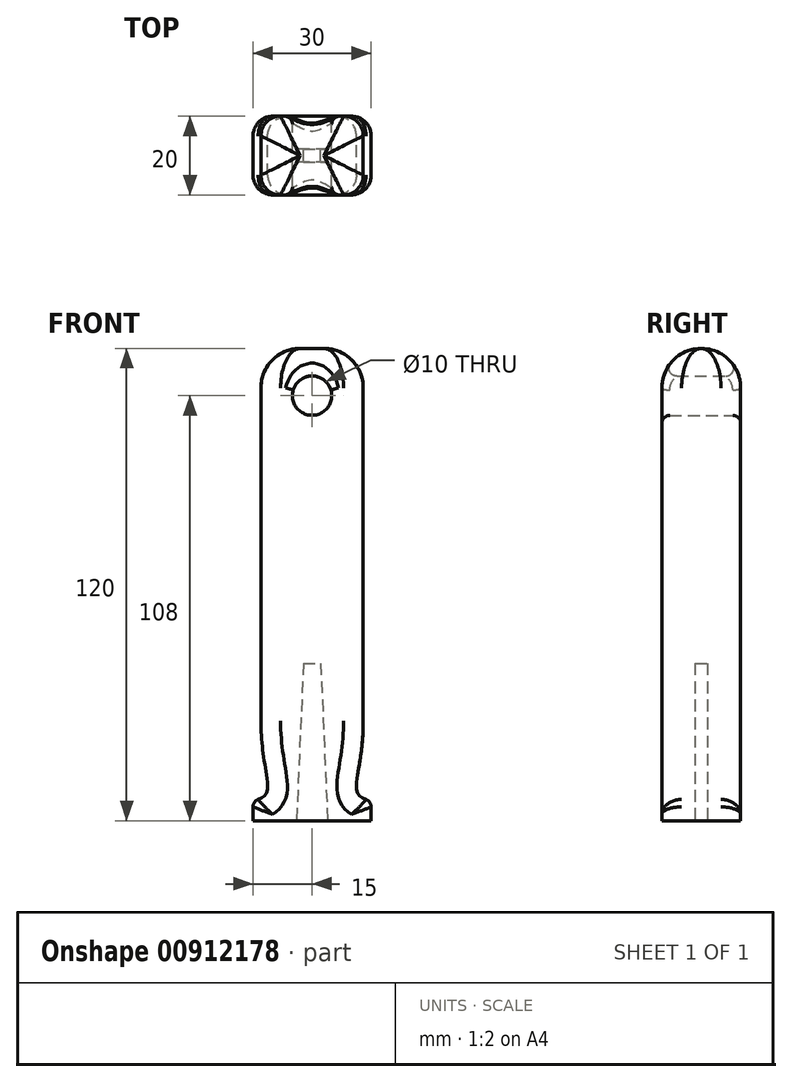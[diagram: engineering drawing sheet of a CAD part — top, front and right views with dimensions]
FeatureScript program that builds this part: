
annotation { "Feature Type Name" : "Feature", "Feature Type Description" : "" }
export const myFeature = defineFeature(function(context is Context, id is Id, definition is map)
    precondition{}
    {
        {
            assignVariable(context, id + "F0", {"name" : "thick", "anyValue" : 3});
        }
        {
            assignVariable(context, id + "F1", {"name" : "margin", "anyValue" : 0.2});
        }
        {
            var Q0;
            Q0=qCreatedBy(makeId("Front.planeOp"),FACE);
            var sketch = newSketch(context, id + "F2", { "sketchPlane" : qUnion([Q0])});
            skLineSegment(sketch, "E0", {"start": v(0, 0) * mm, "end": v(3.95, 0) * mm});
            skLineSegment(sketch, "E1", {"start": v(0, 0) * mm, "end": v(0, 40) * mm, "construction": true});
            skLineSegment(sketch, "E2", {"start": v(0, 40) * mm, "end": v(2.2, 40) * mm});
            skLineSegment(sketch, "E3", {"start": v(2.2, 40) * mm, "end": v(3.95, 0) * mm});
            skLineSegment(sketch, "E4.MirrorCS", {"start": v(0, 40) * mm, "end": v(-2.2, 40) * mm});
            skLineSegment(sketch, "E5.MirrorCS", {"start": v(-2.2, 40) * mm, "end": v(-3.95, 0) * mm});
            skLineSegment(sketch, "E6.MirrorCS", {"start": v(0, 0) * mm, "end": v(-3.95, 0) * mm});
            skSolve(sketch);
        }
        {
            var Q0;
            Q0=qCreatedBy(makeId("Front.planeOp"),FACE);
            var sketch = newSketch(context, id + "F3", { "sketchPlane" : qUnion([Q0])});
            skLineSegment(sketch, "E7", {"start": v(0, 0) * mm, "end": v(0, 120) * mm, "construction": true});
            skLineSegment(sketch, "E8", {"start": v(0, 0) * mm, "end": v(15, 0) * mm});
            skLineSegment(sketch, "E9", {"start": v(15, 0) * mm, "end": v(15, 5) * mm});
            skLineSegment(sketch, "E10", {"start": v(0, 120) * mm, "end": v(13, 120) * mm});
            skLineSegment(sketch, "E11", {"start": v(13, 120) * mm, "end": v(13, 25.33) * mm});
            skFitSpline(sketch, "E12", {"points": [v(13, 25.33) * mm, v(11.35, 7.71) * mm, v(15, 5) * mm], "startDerivative": vector(0, -41.02) * mm, "endDerivative": vector(21.38, -5.71) * mm});
            skFitSpline(sketch, "E13.MirrorCS", {"points": [v(-13, 25.33) * mm, v(-11.35, 7.71) * mm, v(-15, 5) * mm], "startDerivative": vector(0, -41.02) * mm, "endDerivative": vector(-21.38, -5.71) * mm});
            skLineSegment(sketch, "E14.MirrorCS", {"start": v(0, 0) * mm, "end": v(-15, 0) * mm});
            skLineSegment(sketch, "E15.MirrorCS", {"start": v(0, 120) * mm, "end": v(-13, 120) * mm});
            skLineSegment(sketch, "E16.MirrorCS", {"start": v(-15, 0) * mm, "end": v(-15, 5) * mm});
            skLineSegment(sketch, "E17.MirrorCS", {"start": v(-13, 120) * mm, "end": v(-13, 25.33) * mm});
            skLineSegment(sketch, "E18", {"start": v(0, 120) * mm, "end": v(0, 108) * mm, "construction": true});
            skCircle(sketch, "E19", {"center": v(0, 108) * mm, "radius": 5 * mm});
            skSolve(sketch);
        }
        {
            var Q0;
            Q0=makeQuery(id+"F3.imprint","IMPRINT",FACE,{"disambiguationData":[TD([[makeQuery(id+"F3.imprint","IMPRINT",EDGE,{"derivedFrom":sQuery(id+"F3.wireOp",EDGE,"E8")}),1.0]])]});
            extrude(context, id + "F4", {"entities" : qUnion([Q0]), "endBound" : BoundingType.SYMMETRIC, "depth" : 20 * mm, "offsetDistance" : 25 * mm});
        }
        {
            var Q0;
            Q0 = qSketchRegion(id + "F2", true);
            extrude(context, id + "F5", {"entities" : qUnion([Q0]), "operationType" : NewBodyOperationType.REMOVE, "endBound" : BoundingType.SYMMETRIC, "depth" : (getVariable(context, 'thick') + getVariable(context, 'margin')) * mm, "offsetDistance" : 25 * mm});
        }
        {
            var Q0;
            Q0=makeQuery(id+"F4.opExtrude","SWEPT_FACE",FACE,{"disambiguationData":[OSD([sQuery(id+"F3.wireOp",EDGE,"E10"),sQuery(id+"F3.wireOp",EDGE,"E15.MirrorCS")])]});
            fillet(context, id + "F6", {"entities" : qUnion([Q0]), "radius" : 10 * mm, "tangentPropagation" : true, "allowEdgeOverflow" : false});
        }
        {
            var Q0;
            Q0=makeQuery(id+"F4.opExtrude","CAP_EDGE",EDGE,{"disambiguationData":[OSD([sQuery(id+"F3.wireOp",EDGE,"E11")])],"isStart":false});
            var Q1;
            Q1=makeQuery(id+"F4.opExtrude","CAP_EDGE",EDGE,{"disambiguationData":[OSD([sQuery(id+"F3.wireOp",EDGE,"E17.MirrorCS")])],"isStart":false});
            var Q2;
            Q2=makeQuery(id+"F4.opExtrude","CAP_EDGE",EDGE,{"disambiguationData":[OSD([sQuery(id+"F3.wireOp",EDGE,"E11")])],"isStart":true});
            var Q3;
            Q3=makeQuery(id+"F4.opExtrude","CAP_EDGE",EDGE,{"disambiguationData":[OSD([sQuery(id+"F3.wireOp",EDGE,"E17.MirrorCS")])],"isStart":true});
            var Q4;
            Q4=makeQuery(id+"F4.opExtrude","CAP_EDGE",EDGE,{"disambiguationData":[OSD([sQuery(id+"F3.wireOp",EDGE,"E9")])],"isStart":false});
            var Q5;
            Q5=makeQuery(id+"F4.opExtrude","CAP_EDGE",EDGE,{"disambiguationData":[OSD([sQuery(id+"F3.wireOp",EDGE,"E9")])],"isStart":true});
            var Q6;
            Q6=makeQuery(id+"F4.opExtrude","CAP_EDGE",EDGE,{"disambiguationData":[OSD([sQuery(id+"F3.wireOp",EDGE,"E16.MirrorCS")])],"isStart":true});
            var Q7;
            Q7=makeQuery(id+"F4.opExtrude","CAP_EDGE",EDGE,{"disambiguationData":[OSD([sQuery(id+"F3.wireOp",EDGE,"E16.MirrorCS")])],"isStart":false});
            fillet(context, id + "F7", {"entities" : qUnion([Q0, Q1, Q2, Q3, Q4, Q5, Q6, Q7]), "radius" : 5 * mm, "tangentPropagation" : true, "allowEdgeOverflow" : false});
        }
        {
            var Q0;
            Q0=makeQuery(id+"F4.opExtrude","SWEPT_FACE",FACE,{"disambiguationData":[OSD([sQuery(id+"F3.wireOp",EDGE,"E19")])]});
            var Q1;
            Q1=makeQuery(id+"F4.opExtrude","SWEPT_EDGE",EDGE,{"disambiguationData":[OSD([sQuery(id+"F3.wireOp",EDGE,"E13.MirrorCS"),sQuery(id+"F3.wireOp",EDGE,"E16.MirrorCS")])]});
            var Q2;
            Q2=makeQuery(id+"F4.opExtrude","SWEPT_EDGE",EDGE,{"disambiguationData":[OSD([sQuery(id+"F3.wireOp",EDGE,"E9"),sQuery(id+"F3.wireOp",EDGE,"E12")])]});
            fillet(context, id + "F8", {"entities" : qUnion([Q0, Q1, Q2]), "radius" : 2 * mm, "tangentPropagation" : true, "allowEdgeOverflow" : false});
        }
    });
